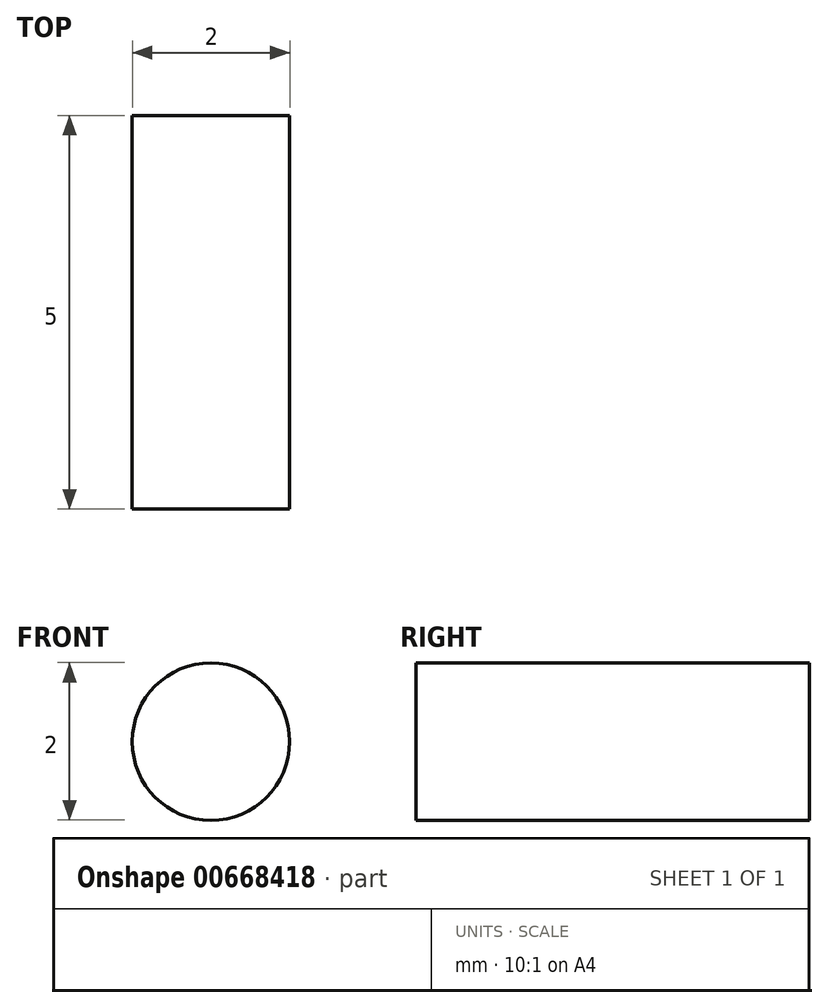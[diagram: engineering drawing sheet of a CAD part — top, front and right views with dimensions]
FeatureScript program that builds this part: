
annotation { "Feature Type Name" : "Feature", "Feature Type Description" : "" }
export const myFeature = defineFeature(function(context is Context, id is Id, definition is map)
    precondition{}
    {
        {
            var Q0;
            Q0=qCreatedBy(makeId("Front.planeOp"),FACE);
            var sketch = newSketch(context, id + "F0", { "sketchPlane" : qUnion([Q0])});
            skCircle(sketch, "E0", {"center": v(-21.81, 21.53) * mm, "radius": 1 * mm});
            skSolve(sketch);
        }
        {
            var Q0;
            Q0=makeQuery(id+"F0.imprint","IMPRINT",FACE,{"disambiguationData":[TD([[makeQuery(id+"F0.imprint","IMPRINT",EDGE,{"derivedFrom":sQuery(id+"F0.wireOp",EDGE,"E0")}),1.0]])]});
            extrude(context, id + "F1", {"entities" : qUnion([Q0]), "depth" : 5 * mm, "offsetDistance" : 25 * mm});
        }
    });
